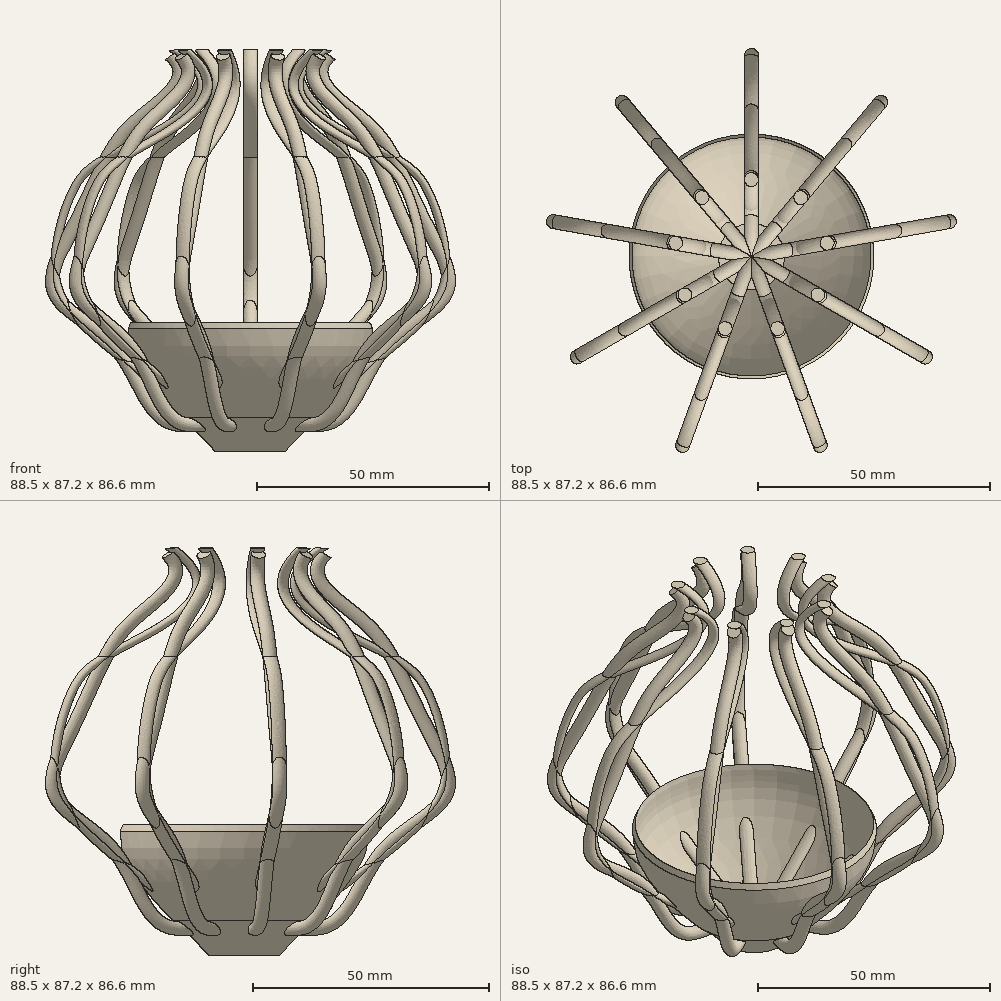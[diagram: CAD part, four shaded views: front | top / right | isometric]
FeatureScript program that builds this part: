
annotation { "Feature Type Name" : "Feature", "Feature Type Description" : "" }
export const myFeature = defineFeature(function(context is Context, id is Id, definition is map)
    precondition{}
    {
        {
            var Q0;
            Q0=qCreatedBy(makeId("Top.planeOp"),FACE);
            var sketch = newSketch(context, id + "F0", { "sketchPlane" : qUnion([Q0])});
            skCircle(sketch, "E0", {"center": v(0, 0) * mm, "radius": 1.5 * mm});
            skSolve(sketch);
        }
        {
            var Q0;
            Q0=qCreatedBy(makeId("Right.planeOp"),FACE);
            var sketch = newSketch(context, id + "F1", { "sketchPlane" : qUnion([Q0])});
            skFitSpline(sketch, "E1", {"points": [v(0, 0) * mm, v(42.81, 40.05) * mm, v(38.83, 56.16) * mm, v(27.31, 65.52) * mm, v(16.58, 86.54) * mm], "startDerivative": vector(290.92, 201.13) * mm, "endDerivative": vector(183.6, 119.68) * mm});
            skSolve(sketch);
        }
        {
            var Q0;
            Q0=makeQuery(id+"F0.imprint","IMPRINT",FACE,{"disambiguationData":[TD([[makeQuery(id+"F0.imprint","IMPRINT",EDGE,{"derivedFrom":sQuery(id+"F0.wireOp",EDGE,"E0")}),1.0]])]});
            var Q1;
            Q1=sQuery(id+"F1.wireOp",EDGE,"E1");
            sweep(context, id + "F2", {"profiles" : qUnion([Q0]), "path" : qUnion([Q1])});
        }
        {
            var Q0;
            Q0=qCreatedBy(makeId("Right.planeOp"),FACE);
            var sketch = newSketch(context, id + "F3", { "sketchPlane" : qUnion([Q0])});
            skLineSegment(sketch, "E2", {"start": v(0, 75.03) * mm, "end": v(0, 0) * mm});
            skSolve(sketch);
        }
        {
            var Q0;
            Q0=makeQuery(id+"F2.opSweep","SWEPT_BODY",BODY,{"disambiguationData":[OSD([sQuery(id+"F0.wireOp",EDGE,"E0"),sQuery(id+"F1.wireOp",EDGE,"E1")])]});
            var Q1;
            Q1=sQuery(id+"F3.wireOp",EDGE,"E2");
            circularPattern(context, id + "F4", {"entities" : qUnion([Q0]), "axis" : qUnion([Q1]), "angle" : 360 * degree, "instanceCount" : 9, "equalSpace" : true});
        }
        {
            var Q0;
            Q0=qCreatedBy(makeId("Right.planeOp"),FACE);
            var sketch = newSketch(context, id + "F5", { "sketchPlane" : qUnion([Q0])});
            skFitSpline(sketch, "E3", {"points": [v(0, 0) * mm, v(17.02, 6) * mm, v(29.26, 21.88) * mm, v(43.09, 34.55) * mm, v(37.61, 50.61) * mm, v(27.94, 68.31) * mm, v(17.5, 77.66) * mm, v(17.25, 85.2) * mm], "startDerivative": vector(42.57, 179.92) * mm, "endDerivative": vector(87.87, 82.93) * mm});
            skSolve(sketch);
        }
        {
            var Q0;
            Q0=makeQuery(id+"F0.imprint","IMPRINT",FACE,{"disambiguationData":[TD([[makeQuery(id+"F0.imprint","IMPRINT",EDGE,{"derivedFrom":sQuery(id+"F0.wireOp",EDGE,"E0")}),1.0]])]});
            var Q1;
            Q1=sQuery(id+"F5.wireOp",EDGE,"E3");
            sweep(context, id + "F6", {"profiles" : qUnion([Q0]), "path" : qUnion([Q1])});
        }
        {
            var Q0;
            Q0=makeQuery(id+"F6.opSweep","SWEPT_BODY",BODY,{"disambiguationData":[OSD([sQuery(id+"F0.wireOp",EDGE,"E0"),sQuery(id+"F5.wireOp",EDGE,"E3")])]});
            var Q1;
            Q1=sQuery(id+"F3.wireOp",EDGE,"E2");
            circularPattern(context, id + "F7", {"entities" : qUnion([Q0]), "axis" : qUnion([Q1]), "angle" : 360 * degree, "instanceCount" : 9, "equalSpace" : true});
        }
        {
            var Q0;
            Q0=qCreatedBy(makeId("Right.planeOp"),FACE);
            var sketch = newSketch(context, id + "F8", { "sketchPlane" : qUnion([Q0])});
            skLineSegment(sketch, "E4", {"start": v(0, 0) * mm, "end": v(-7.66, 0) * mm});
            skFitSpline(sketch, "E5", {"points": [v(-7.66, 0) * mm, v(-25.94, 22.25) * mm, v(-27.34, 28.92) * mm, v(-39.38, 32.39) * mm, v(-43.99, 39.72) * mm, v(-28.52, 49.34) * mm, v(-25.94, 53.99) * mm, v(-27.88, 60.6) * mm, v(-19.36, 63.15) * mm, v(-10.59, 67.4) * mm, v(-5.43, 73.09) * mm, v(-16.7, 85.23) * mm, v(-9.56, 87.28) * mm], "startDerivative": vector(-195.82, 182.27) * mm, "endDerivative": vector(76.65, 14.98) * mm});
            skLineSegment(sketch, "E6", {"start": v(0, 1.12) * mm, "end": v(0, 0) * mm});
            skLineSegment(sketch, "E7", {"start": v(0, 0) * mm, "end": v(0, 33.32) * mm});
            skLineSegment(sketch, "E8", {"start": v(0, 33.32) * mm, "end": v(0, 27.78) * mm, "construction": true});
            skPoint(sketch, "E9.end.orphan", {"position": v(0, 1.12) * mm});
            skFitSpline(sketch, "E10.trimOffspring", {"points": [v(-7.66, 0) * mm, v(-16.57, 8.29) * mm, v(-28.24, 20.15) * mm, v(-24.9, 30.9) * mm, v(-40.07, 30.29) * mm, v(-48.65, 41.49) * mm, v(-27.66, 48.35) * mm, v(-24.61, 53.6) * mm, v(-30.98, 62.36) * mm, v(-18.05, 62.36) * mm, v(-11.64, 67.18) * mm, v(0.35, 72.83) * mm, v(-24.07, 86.76) * mm, v(-11.33, 86.93) * mm, v(-9.56, 87.28) * mm]});
            skPoint(sketch, "E11.end.orphan", {"position": v(0, 0.56) * mm});
            skFitSpline(sketch, "E12.0", {"points": [v(-7.12, 0.59) * mm, v(-9.15, 2.48) * mm, v(-13.11, 6.24) * mm, v(-17.45, 10.73) * mm, v(-20.37, 14.14) * mm, v(-22.22, 16.58) * mm, v(-23.46, 18.5) * mm, v(-24.23, 19.96) * mm, v(-24.7, 21.01) * mm, v(-25.06, 22.01) * mm, v(-25.3, 22.95) * mm, v(-25.43, 23.87) * mm, v(-25.54, 25.07) * mm, v(-25.57, 26.2) * mm, v(-25.7, 27.3) * mm, v(-25.88, 28.1) * mm, v(-26.17, 28.73) * mm, v(-26.5, 29.2) * mm, v(-26.81, 29.53) * mm, v(-27.17, 29.82) * mm, v(-27.68, 30.14) * mm, v(-28.4, 30.47) * mm, v(-29.36, 30.77) * mm, v(-30.75, 31.11) * mm, v(-32.66, 31.46) * mm, v(-35.1, 31.9) * mm, v(-37.08, 32.37) * mm, v(-38.56, 32.9) * mm, v(-39.93, 33.51) * mm, v(-41.44, 34.5) * mm, v(-42.77, 35.89) * mm, v(-43.38, 37.1) * mm, v(-43.55, 38.01) * mm, v(-43.51, 38.68) * mm, v(-43.35, 39.23) * mm, v(-43.11, 39.68) * mm, v(-42.8, 40.14) * mm, v(-42.28, 40.74) * mm, v(-41.18, 41.7) * mm, v(-39.39, 42.9) * mm, v(-36.82, 44.3) * mm, v(-34.08, 45.61) * mm, v(-31.39, 46.88) * mm, v(-29.38, 47.9) * mm, v(-28.02, 48.7) * mm, v(-27.14, 49.3) * mm, v(-26.4, 49.93) * mm, v(-25.8, 50.6) * mm, v(-25.36, 51.32) * mm, v(-25.08, 52.1) * mm, v(-24.99, 52.94) * mm, v(-25.06, 53.79) * mm, v(-25.28, 54.66) * mm, v(-25.6, 55.53) * mm, v(-25.99, 56.4) * mm, v(-26.38, 57.25) * mm, v(-26.74, 58.07) * mm, v(-27.03, 58.83) * mm, v(-27.17, 59.38) * mm, v(-27.22, 59.75) * mm, v(-27.22, 59.97) * mm, v(-27.2, 60.15) * mm, v(-27.16, 60.28) * mm, v(-27.1, 60.39) * mm, v(-26.98, 60.51) * mm, v(-26.82, 60.65) * mm, v(-26.52, 60.83) * mm, v(-26, 61.06) * mm, v(-25.2, 61.29) * mm, v(-23.96, 61.55) * mm, v(-22.53, 61.77) * mm, v(-21.04, 62) * mm, v(-19.93, 62.2) * mm, v(-18.84, 62.44) * mm, v(-17.82, 62.74) * mm, v(-16.87, 63.09) * mm, v(-15.66, 63.6) * mm, v(-14.24, 64.32) * mm, v(-12.88, 65.12) * mm, v(-11.79, 65.78) * mm, v(-10.94, 66.28) * mm, v(-10.08, 66.78) * mm, v(-9.15, 67.3) * mm, v(-8.2, 67.83) * mm, v(-7.29, 68.4) * mm, v(-6.42, 69) * mm, v(-5.65, 69.68) * mm, v(-5, 70.45) * mm, v(-4.56, 71.35) * mm, v(-4.45, 72.22) * mm, v(-4.54, 72.94) * mm, v(-4.7, 73.48) * mm, v(-4.95, 74.01) * mm, v(-5.37, 74.7) * mm, v(-6.03, 75.56) * mm, v(-7.01, 76.6) * mm, v(-8.5, 78.01) * mm, v(-10.16, 79.42) * mm, v(-11.8, 80.79) * mm, v(-12.98, 81.77) * mm, v(-14.03, 82.7) * mm, v(-14.91, 83.56) * mm, v(-15.45, 84.2) * mm, v(-15.73, 84.6) * mm, v(-15.87, 84.87) * mm, v(-15.92, 85.04) * mm, v(-15.92, 85.1) * mm, v(-15.92, 85.1) * mm, v(-15.92, 85.1) * mm, v(-15.9, 85.14) * mm, v(-15.8, 85.24) * mm, v(-15.6, 85.37) * mm, v(-15.32, 85.5) * mm, v(-14.85, 85.67) * mm, v(-14.12, 85.85) * mm, v(-13.12, 86.03) * mm, v(-12.08, 86.16) * mm, v(-11.06, 86.27) * mm, v(-10.14, 86.37) * mm, v(-9.63, 86.45) * mm, v(-9.4, 86.5) * mm]});
            skFitSpline(sketch, "E13", {"points": [v(-9.56, 87.28) * mm, v(-9.12, 86.94) * mm, v(-9.4, 86.5) * mm], "startDerivative": vector(1.22, -0.6) * mm, "endDerivative": vector(-0.92, -0.97) * mm});
            skLineSegment(sketch, "E14", {"start": v(-7.12, 0.59) * mm, "end": v(0, 0.56) * mm});
            skSolve(sketch);
        }
        {
            var Q0;
            {var subQ0=sQuery(id+"F8.wireOp",EDGE,"E4");Q0=makeQuery(id+"F8.imprint","IMPRINT",FACE,{"disambiguationData":[TD([[makeQuery(id+"F8.imprint","IMPRINT",EDGE,{"derivedFrom":subQ0}),-1.0]])]});}
            var Q1;
            Q1=sQuery(id+"F8.wireOp",EDGE,"E7");
            revolve(context, id + "F9", {"entities" : qUnion([Q0]), "axis" : qUnion([Q1]), "revolveType" : RevolveType.FULL});
        }
    });
